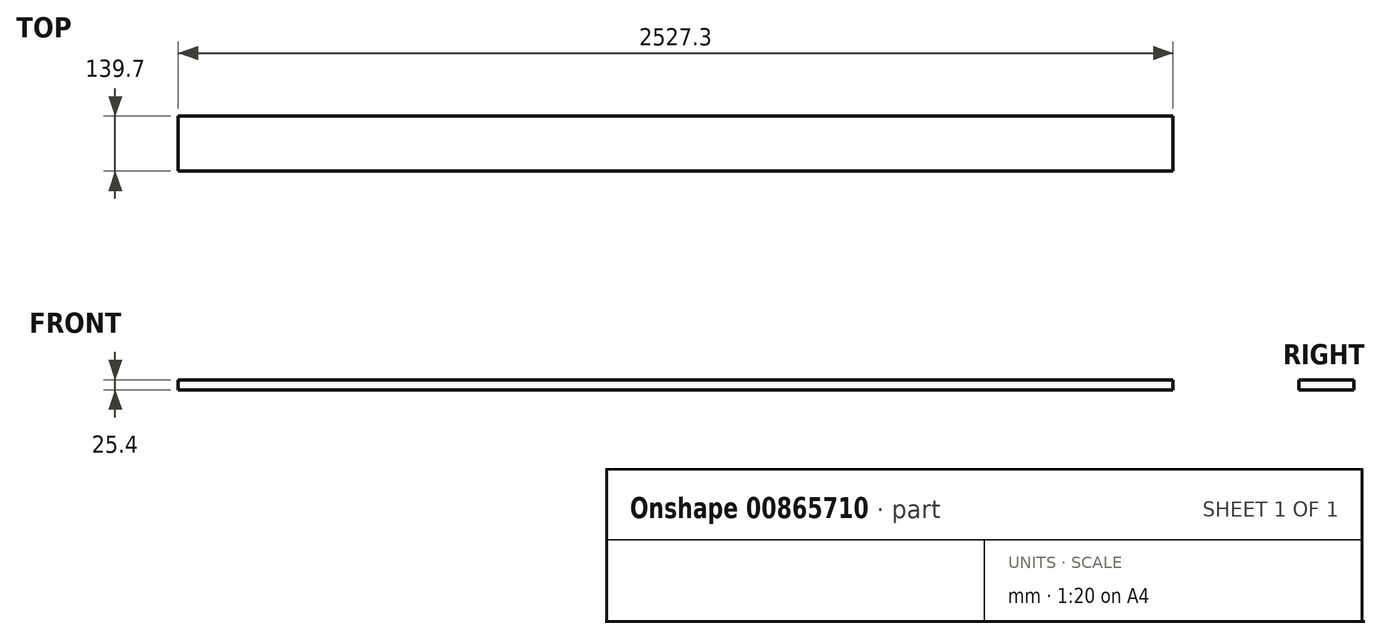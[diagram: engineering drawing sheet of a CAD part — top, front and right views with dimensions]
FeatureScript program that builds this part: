
annotation { "Feature Type Name" : "Feature", "Feature Type Description" : "" }
export const myFeature = defineFeature(function(context is Context, id is Id, definition is map)
    precondition{}
    {
        {
            var Q0;
            Q0=qCreatedBy(makeId("Right.planeOp"),FACE);
            var sketch = newSketch(context, id + "F0", { "sketchPlane" : qUnion([Q0])});
            skLineSegment(sketch, "E0.bottom", {"start": v(0, 0) * mm, "end": v(139.7, 0) * mm});
            skLineSegment(sketch, "E0.top", {"start": v(0, 25.4) * mm, "end": v(139.7, 25.4) * mm});
            skLineSegment(sketch, "E0.left", {"start": v(0, 0) * mm, "end": v(0, 25.4) * mm});
            skLineSegment(sketch, "E0.right", {"start": v(139.7, 0) * mm, "end": v(139.7, 25.4) * mm});
            skSolve(sketch);
        }
        {
            var Q0;
            Q0=makeQuery(id+"F0.imprint","IMPRINT",FACE,{"disambiguationData":[TD([[makeQuery(id+"F0.imprint","IMPRINT",EDGE,{"derivedFrom":sQuery(id+"F0.wireOp",EDGE,"E0.bottom")}),1.0]])]});
            extrude(context, id + "F1", {"entities" : qUnion([Q0]), "depth" : 2527.3 * mm, "offsetDistance" : 25.4 * mm});
        }
    });
